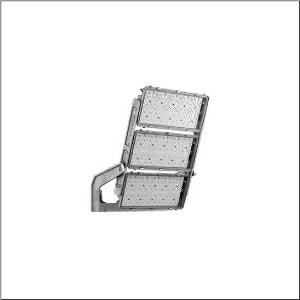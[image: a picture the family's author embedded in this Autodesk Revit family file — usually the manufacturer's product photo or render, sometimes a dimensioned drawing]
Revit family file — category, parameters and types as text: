
# Revit family: floodlight_fl_11_maxi_pro_remote___pl64_5xa779524e01ba_e2b2
name_source: partatom
category: Lighting Fixtures
units: mm (PartAtom-declared; Revit-internal decimal feet)

## family parameters
Cut with Voids When Loaded = No
Host = Face
Light Source = No
Part Type = Normal
Room Calculation Point = No
Round Connector Dimension = Use Diameter
Shared = No

## types (1)
- --- (1 x LED, 107650 lm, 1020.5 W, 5700K)
    Apparent Load = 1020 VA
    CIE Flux Codes = 28 80 98 100 100
    Color Rendering = 90
    Color Temperature = 5700K
    Default Elevation = 1800 mm
    Description = Floodlight FL 11  maxi  pro Remote floodlight; light control with lens of PMMA; cover panel of toughened safety glass, transparent; light distribution: PL64, asymmetric direct distribution, LEDcolour temperature: 5700K, rated luminous flux: 107.650lm, colour rendering: CRI > 90, light colour: 957; luminous efficacy: 105lm/W; brightness control: DMX+RDM; with terminal, 8-pole, max. 2.5mm², mains connection: 220..240V/380..400V AC, 50/60Hz, surge voltage resistance: line to ground: 10kV, ECG replaceable separately, LED unit replaceable without ESD environment, dustproof LED module, dimming range 10..100%; 1021W reduction: 440W; floodlight with 3x LED unit of diecast aluminium, coated grey; length: 713mm / width: 651mm / height: 338mm; housing frame, of diecast aluminium, uncoated, natural, mounting bracket, of diecast aluminium, uncoated, natural, equipment: Longlife, protection rating (complete): IP66; insulation class (complete): insulation class I (protective earthing); certification: CE, ENEC, VDE; ball protection: ball impact resistance with accessories, only for outdoor installations, rated ambient temperature 10°C, permissible operating ambient temperature: -40..+40°C, permissible storage temperature: -40..+85°C; packaging unit: 1 piece

Light Distribution: PL64
    Height = 320 mm
    Lamp = 1 x LED
    Lamp Light Flux = 107650 lm
    Lamp Power = 1020.5 W
    Lamp count = 1
    Length = 1002 mm
    Luminous efficacy = 105 lm/W
    Manufacturer = Siteco
    ModVariant = No
    Model = 5XA779524E01BA
    Number of Poles = 1
    OnlyDefault = Yes
    Power Factor = 1
    Product Name = Floodlight FL 11 maxi pro Remote | PL64
    Product group = floodlight | pylon top
    ProductGroupID = 6101
    Protection Class = Protection class I
    Protection Degree = IP 66
    RLX_Detail_Level = 1
    RlxData = <blob elided: 52433 chars, md5=446bb234>
    Socket = socket
    Standby Power = 0 W
    System Light Flux = 107650 lm
    System Power = 1020 W
    Type Comments = factory setting: luminous flux: 100 % | dim-lin: 255 | 710 mA
    Type Image = l_1006784.jpg
    URL = http://relux.com
    VarID = @adj_006875
    Voltage = 0 V
    Weight = 0.00 kg
    Width = 655 mm

## geometry (parser evidence)
native form markers: Blend x4, Sweep x14
no freeform markers — native parametric forms only
